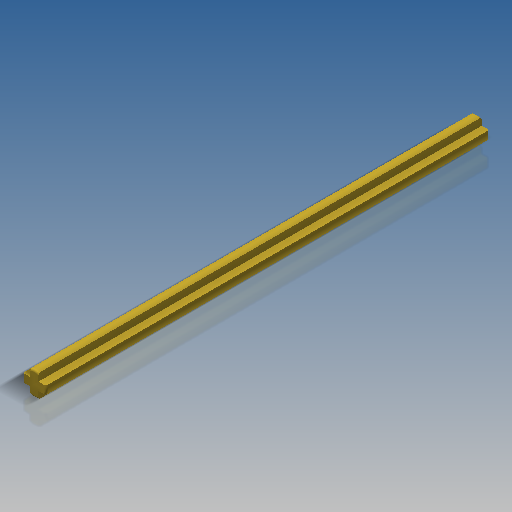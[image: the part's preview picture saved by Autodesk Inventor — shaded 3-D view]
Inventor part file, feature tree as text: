
AUTODESK INVENTOR PART (.ipt)
format: ipt  version: 2019.4 (Build 234330000, 330)  size: 160,256 bytes
history: native  units: in
note: dims shown in document units (in); Inventor stores cm internally (conversion verified against a paired STEP export)
features: extrude x1, fillet x1, sketch x1
ambient origin geometry x8: Origin, YZ Plane, XZ Plane, XY Plane, X Axis, Y Axis, Z Axis, Center Point
bodies: Solid1 (feature_tree)
feature tree (3):
  extrude  "Extrusion1"  Depth=0.0157in
  fillet  "Fillet1"  Radius=3.4646in
  sketch  "Sketch1"  dims[d0=0.189in d1=0.063in d2=3.4646in d3=0.0in d4=0.0157in d5=0.0in d6=0.0in]
